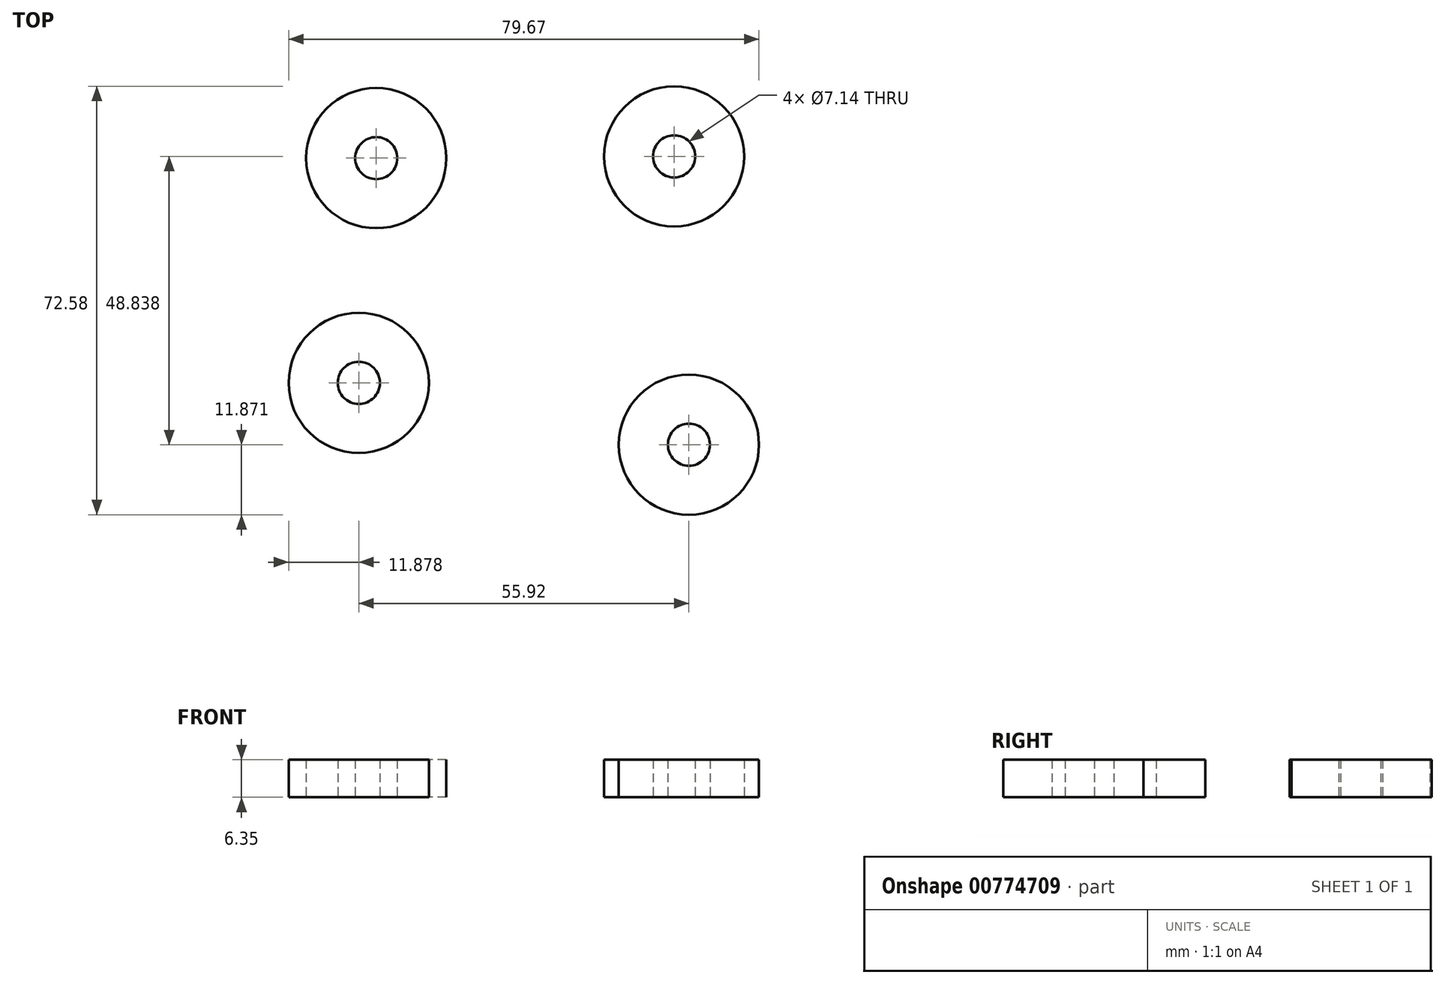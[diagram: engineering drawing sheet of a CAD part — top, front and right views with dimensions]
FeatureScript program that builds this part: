
annotation { "Feature Type Name" : "Feature", "Feature Type Description" : "" }
export const myFeature = defineFeature(function(context is Context, id is Id, definition is map)
    precondition{}
    {
        {
            var Q0;
            Q0=qCreatedBy(makeId("Top.planeOp"),FACE);
            var sketch = newSketch(context, id + "F0", { "sketchPlane" : qUnion([Q0])});
            skCircle(sketch, "E0", {"center": v(-38.4, 32.15) * mm, "radius": 11.87 * mm});
            skCircle(sketch, "E1", {"center": v(-41.35, -5.91) * mm, "radius": 11.87 * mm});
            skCircle(sketch, "E2", {"center": v(12.06, 32.45) * mm, "radius": 11.87 * mm});
            skCircle(sketch, "E3", {"center": v(14.57, -16.39) * mm, "radius": 11.87 * mm});
            skCircle(sketch, "E4", {"center": v(14.57, -16.39) * mm, "radius": 3.57 * mm});
            skCircle(sketch, "E5", {"center": v(-41.35, -5.91) * mm, "radius": 3.57 * mm});
            skCircle(sketch, "E6", {"center": v(-38.4, 32.15) * mm, "radius": 3.57 * mm});
            skCircle(sketch, "E7", {"center": v(12.06, 32.45) * mm, "radius": 3.57 * mm});
            skSolve(sketch);
        }
        {
            var Q0;
            Q0=makeQuery(id+"F0.imprint","IMPRINT",FACE,{"disambiguationData":[TD([[makeQuery(id+"F0.imprint","IMPRINT",EDGE,{"derivedFrom":sQuery(id+"F0.wireOp",EDGE,"E0")}),1.0]])]});
            var Q1;
            Q1=makeQuery(id+"F0.imprint","IMPRINT",FACE,{"disambiguationData":[TD([[makeQuery(id+"F0.imprint","IMPRINT",EDGE,{"derivedFrom":sQuery(id+"F0.wireOp",EDGE,"E2")}),1.0]])]});
            var Q2;
            Q2=makeQuery(id+"F0.imprint","IMPRINT",FACE,{"disambiguationData":[TD([[makeQuery(id+"F0.imprint","IMPRINT",EDGE,{"derivedFrom":sQuery(id+"F0.wireOp",EDGE,"E3")}),1.0]])]});
            var Q3;
            Q3=makeQuery(id+"F0.imprint","IMPRINT",FACE,{"disambiguationData":[TD([[makeQuery(id+"F0.imprint","IMPRINT",EDGE,{"derivedFrom":sQuery(id+"F0.wireOp",EDGE,"E1")}),1.0]])]});
            extrude(context, id + "F1", {"entities" : qUnion([Q0, Q1, Q2, Q3]), "depth" : 6.35 * mm, "offsetDistance" : 25.4 * mm});
        }
    });
